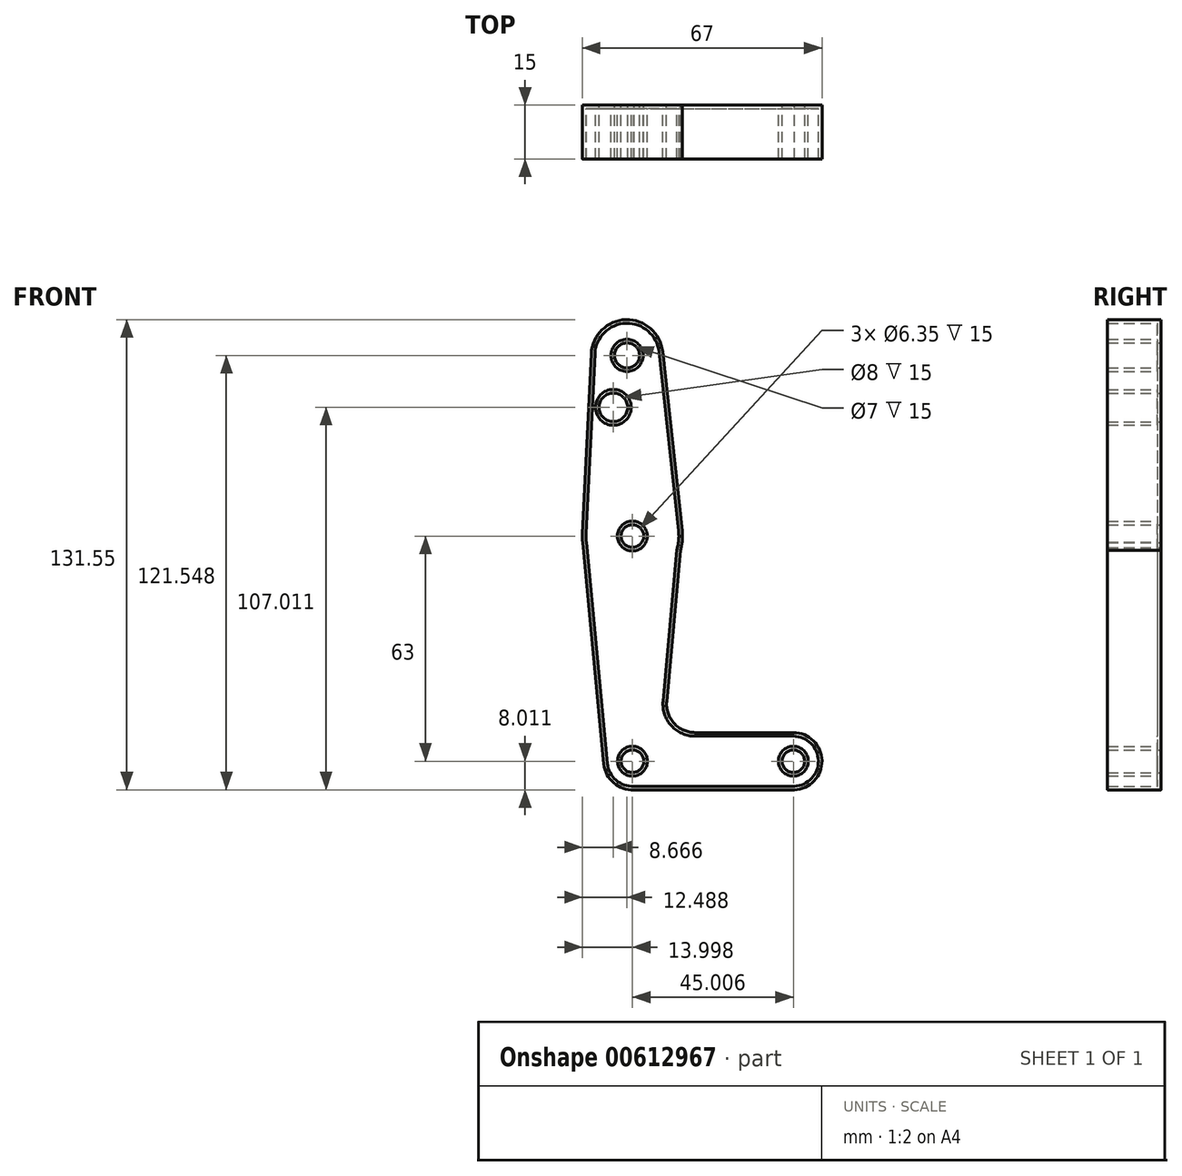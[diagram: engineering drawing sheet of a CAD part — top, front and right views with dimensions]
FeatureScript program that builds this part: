
annotation { "Feature Type Name" : "Feature", "Feature Type Description" : "" }
export const myFeature = defineFeature(function(context is Context, id is Id, definition is map)
    precondition{}
    {
        {
            var Q0;
            Q0=qCreatedBy(makeId("Front.planeOp"),FACE);
            var sketch = newSketch(context, id + "F0", { "sketchPlane" : qUnion([Q0])});
            skArc(sketch, "E0", {"start": v(-136.87, 13.16) * mm, "mid": v(-134.12, 7.85) * mm, "end": v(-128.47, 5.92) * mm});
            skCircle(sketch, "E1", {"center": v(-128.9, 76.92) * mm, "radius": 14 * mm});
            skArc(sketch, "E2", {"start": v(-120.47, 128.55) * mm, "mid": v(-130.71, 137.45) * mm, "end": v(-140.4, 127.95) * mm});
            skCircle(sketch, "E3", {"center": v(-83.9, 13.92) * mm, "radius": 8 * mm});
            skLineSegment(sketch, "E4", {"start": v(-130.41, 127.46) * mm, "end": v(-130.37, 123.96) * mm});
            skLineSegment(sketch, "E5", {"start": v(-128.9, 13.92) * mm, "end": v(-83.9, 13.92) * mm});
            skLineSegment(sketch, "E6", {"start": v(-128.9, 76.92) * mm, "end": v(-128.9, 13.92) * mm});
            skLineSegment(sketch, "E7", {"start": v(-111.37, 21.93) * mm, "end": v(-83.9, 21.92) * mm});
            skLineSegment(sketch, "E8", {"start": v(-140.4, 127.95) * mm, "end": v(-142.89, 77.61) * mm});
            skLineSegment(sketch, "E9", {"start": v(-120.47, 128.55) * mm, "end": v(-114.99, 78.44) * mm});
            skLineSegment(sketch, "E10", {"start": v(-115.49, 72.91) * mm, "end": v(-119.33, 30.65) * mm});
            skCircle(sketch, "E11", {"center": v(-130.41, 127.46) * mm, "radius": 0.32 * mm});
            skCircle(sketch, "E12", {"center": v(-134.23, 112.92) * mm, "radius": 4 * mm});
            skCircle(sketch, "E13", {"center": v(-128.9, 76.92) * mm, "radius": 3.17 * mm});
            skCircle(sketch, "E14", {"center": v(-128.9, 13.92) * mm, "radius": 3.18 * mm});
            skCircle(sketch, "E15", {"center": v(-83.9, 13.92) * mm, "radius": 3.18 * mm});
            skCircle(sketch, "E16", {"center": v(-130.41, 127.46) * mm, "radius": 3.5 * mm});
            skArc(sketch, "E17.filletArc", {"start": v(-119.33, 30.65) * mm, "mid": v(-117.27, 24.53) * mm, "end": v(-111.37, 21.93) * mm});
            skLineSegment(sketch, "E18", {"start": v(-142.78, 75.04) * mm, "end": v(-136.87, 13.16) * mm});
            skLineSegment(sketch, "E19", {"start": v(-128.47, 5.92) * mm, "end": v(-83.6, 5.93) * mm});
            skSolve(sketch);
        }
        {
            var Q0;
            Q0=makeQuery(id+"F0.imprint","IMPRINT",FACE,{"disambiguationData":[TD([[makeQuery(id+"F0.imprint","IMPRINT",EDGE,{"derivedFrom":sQuery(id+"F0.wireOp",EDGE,"E2")}),1.0]])]});
            var Q1;
            {var subQ4=sQuery(id+"F0.wireOp",EDGE,"E1");var subQ6=sQuery(id+"F0.wireOp",EDGE,"E10");var subQ8=makeQuery(id+"F0.imprint","INTERSECT",VERTEX,{"derivedFrom":[subQ4,subQ6]});Q1=makeQuery(id+"F0.imprint","IMPRINT",FACE,{"disambiguationData":[TD([[makeQuery(id+"F0.imprint","IMPRINT",EDGE,{"disambiguationData":[TD([[subQ8,1.0]])],"derivedFrom":subQ4}),1.0]])]});}
            var Q2;
            {var subQ3=sQuery(id+"F0.wireOp",EDGE,"E1");var subQ8=makeQuery(id+"F0.imprint","INTERSECT",VERTEX,{"derivedFrom":[subQ3,sQuery(id+"F0.wireOp",EDGE,"E8")]});Q2=makeQuery(id+"F0.imprint","IMPRINT",FACE,{"disambiguationData":[TD([[makeQuery(id+"F0.imprint","IMPRINT",EDGE,{"disambiguationData":[TD([[subQ8,1.0]])],"derivedFrom":subQ3}),1.0]])]});}
            var Q3;
            {var subQ0=sQuery(id+"F0.wireOp",EDGE,"E18");Q3=makeQuery(id+"F0.imprint","IMPRINT",FACE,{"disambiguationData":[TD([[makeQuery(id+"F0.imprint","IMPRINT",EDGE,{"derivedFrom":subQ0}),1.0]])]});}
            var Q4;
            {var subQ0=sQuery(id+"F0.wireOp",EDGE,"E7");Q4=makeQuery(id+"F0.imprint","IMPRINT",FACE,{"disambiguationData":[TD([[makeQuery(id+"F0.imprint","IMPRINT",EDGE,{"derivedFrom":subQ0}),-1.0]])]});}
            var Q5;
            {var subQ0=sQuery(id+"F0.wireOp",EDGE,"E19");var subQ1=sQuery(id+"F0.wireOp",EDGE,"E0");var subQ2=makeQuery(id+"F0.imprint","INTERSECT",VERTEX,{"disambiguationData":[OD(1.0)],"derivedFrom":[subQ1,subQ0]});Q5=makeQuery(id+"F0.imprint","IMPRINT",FACE,{"disambiguationData":[TD([[makeQuery(id+"F0.imprint","IMPRINT",EDGE,{"disambiguationData":[TD([[subQ2,-1.0]])],"derivedFrom":subQ1}),-1.0]])]});}
            var Q6;
            {var subQ1=sQuery(id+"F0.wireOp",EDGE,"E0");var subQ7=makeQuery(id+"F0.imprint","INTERSECT",VERTEX,{"derivedFrom":[subQ1,sQuery(id+"F0.wireOp",EDGE,"E18")]});Q6=makeQuery(id+"F0.imprint","IMPRINT",FACE,{"disambiguationData":[TD([[makeQuery(id+"F0.imprint","IMPRINT",EDGE,{"disambiguationData":[TD([[subQ7,1.0]])],"derivedFrom":subQ1}),1.0]])]});}
            var Q7;
            {var subQ0=sQuery(id+"F0.wireOp",EDGE,"0d114a29-6e84-44d3-ad43-cd3293e3a87f.trimOffspring");var subQ1=sQuery(id+"F0.wireOp",EDGE,"E0");var subQ2=makeQuery(id+"F0.imprint","INTERSECT",VERTEX,{"derivedFrom":[subQ1,subQ0]});Q7=makeQuery(id+"F0.imprint","IMPRINT",FACE,{"disambiguationData":[TD([[makeQuery(id+"F0.imprint","IMPRINT",EDGE,{"disambiguationData":[TD([[subQ2,1.0]])],"derivedFrom":subQ1}),1.0]])]});}
            var Q8;
            Q8=makeQuery(id+"F0.imprint","IMPRINT",FACE,{"disambiguationData":[TD([[makeQuery(id+"F0.imprint","IMPRINT",EDGE,{"derivedFrom":sQuery(id+"F0.wireOp",EDGE,"E15")}),-1.0]])]});
            extrude(context, id + "F1", {"entities" : qUnion([Q0, Q1, Q2, Q3, Q4, Q5, Q6, Q7, Q8]), "depth" : 15 * mm, "offsetDistance" : 25.4 * mm});
        }
        {
            var Q0;
            Q0=makeQuery(id+"F1.opExtrude","CAP_FACE",FACE,{"disambiguationData":[OSD([sQuery(id+"F0.wireOp",EDGE,"E0"),sQuery(id+"F0.wireOp",EDGE,"E1"),sQuery(id+"F0.wireOp",EDGE,"E2"),sQuery(id+"F0.wireOp",EDGE,"E3"),sQuery(id+"F0.wireOp",EDGE,"E7"),sQuery(id+"F0.wireOp",EDGE,"E8"),sQuery(id+"F0.wireOp",EDGE,"E9"),sQuery(id+"F0.wireOp",EDGE,"E10"),sQuery(id+"F0.wireOp",EDGE,"E12"),sQuery(id+"F0.wireOp",EDGE,"E13"),sQuery(id+"F0.wireOp",EDGE,"E14"),sQuery(id+"F0.wireOp",EDGE,"E15"),sQuery(id+"F0.wireOp",EDGE,"E16"),sQuery(id+"F0.wireOp",EDGE,"E17.filletArc"),sQuery(id+"F0.wireOp",EDGE,"E18"),sQuery(id+"F0.wireOp",EDGE,"E19")])],"isStart":false});
            shell(context, id + "F2", {"entities" : qUnion([Q0]), "thickness" : 1 * mm});
        }
    });
